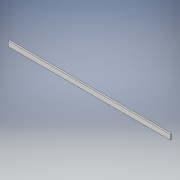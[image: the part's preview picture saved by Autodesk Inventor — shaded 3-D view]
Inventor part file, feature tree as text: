
AUTODESK INVENTOR PART (.ipt)
format: ipt  version: 2018 (Build 220112000, 112)  size: 93,184 bytes
history: native  units: in
note: dims shown in document units (in); Inventor stores cm internally (conversion verified against a paired STEP export)
features: sketch x2, extrude x1
ambient origin geometry x8: Origin, YZ Plane, XZ Plane, XY Plane, X Axis, Y Axis, Z Axis, Center Point
bodies: Solid1 (feature_tree)
feature tree (3):
  sketch  "Sketch1"  dims[d0=19.685in d1=0.5906in]
  extrude  "Extrusion1"  Depth=0.5906in
  sketch  "Sketch2"  dims[d2=0.1969in d3=0.0in]
